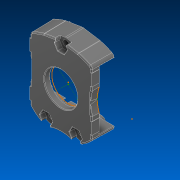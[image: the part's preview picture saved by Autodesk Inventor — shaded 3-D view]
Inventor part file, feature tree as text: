
AUTODESK INVENTOR PART (.ipt)
format: ipt  version: 2022.2 (Build 262287000, 287)  size: 3,665,920 bytes
history: native  units: in
note: dims shown in document units (in); Inventor stores cm internally (conversion verified against a paired STEP export)
features: projected_geometry x26, extrude x5, sketch x4, chamfer x1
ambient origin geometry x8: Origin, YZ Plane, XZ Plane, XY Plane, X Axis, Y Axis, Z Axis, Center Point
bodies: Solid1 (feature_tree)
feature tree (36):
  sketch  "Sketch1"  dims[d0=1.0in d1=0.0in d2=1.125in]
  extrude  "Extrusion1"  Depth=1.125in
  extrude  "Extrusion2"  Depth=0.1in TaperAngle=0.0deg
  extrude  "Extrusion3"  Depth=1.0in TaperAngle=0.0deg
  sketch  "Sketch7"
  extrude  "Extrusion4"  [1 undecoded]
  extrude  "Extrusion5"  [1 undecoded]
  projected_geometry  "Projected Loop1"
  sketch  "Sketch4"  dims[d3=0.1in d4=0.0in d5=0.1in d6=0.0in]
  projected_geometry  "Projected Loop32"
  projected_geometry  "Projected Loop33"
  sketch  "Sketch5"  dims[d7=0.05in d8=0.0in d9=1.0in d10=0.0in]
  projected_geometry  "Projected Loop34"
  projected_geometry  "Projected Loop35"
  projected_geometry  "Projected Loop36"
  projected_geometry  "Projected Loop37"
  projected_geometry  "Projected Loop38"
  projected_geometry  "Projected Loop39"
  projected_geometry  "Projected Loop40"
  projected_geometry  "Projected Loop41"
  projected_geometry  "Projected Loop42"
  projected_geometry  "Projected Loop43"
  projected_geometry  "Projected Loop44"
  projected_geometry  "Projected Loop45"
  projected_geometry  "Projected Loop46"
  projected_geometry  "Projected Loop47"
  projected_geometry  "Projected Loop48"
  projected_geometry  "Projected Loop49"
  projected_geometry  "Projected Loop50"
  projected_geometry  "Projected Loop51"
  projected_geometry  "Projected Loop52"
  projected_geometry  "Projected Loop53"
  projected_geometry  "Projected Loop54"
  chamfer  "Chamfer2"  [1 undecoded]
  projected_geometry  "Project Cut Edges1"
  projected_geometry  "Project Cut Edges2"
note: 3 required parameter values undecoded (feature->parameter linkage not recoverable at this tier; creation-order binding heuristic only, values carry confidence <= 0.55)
